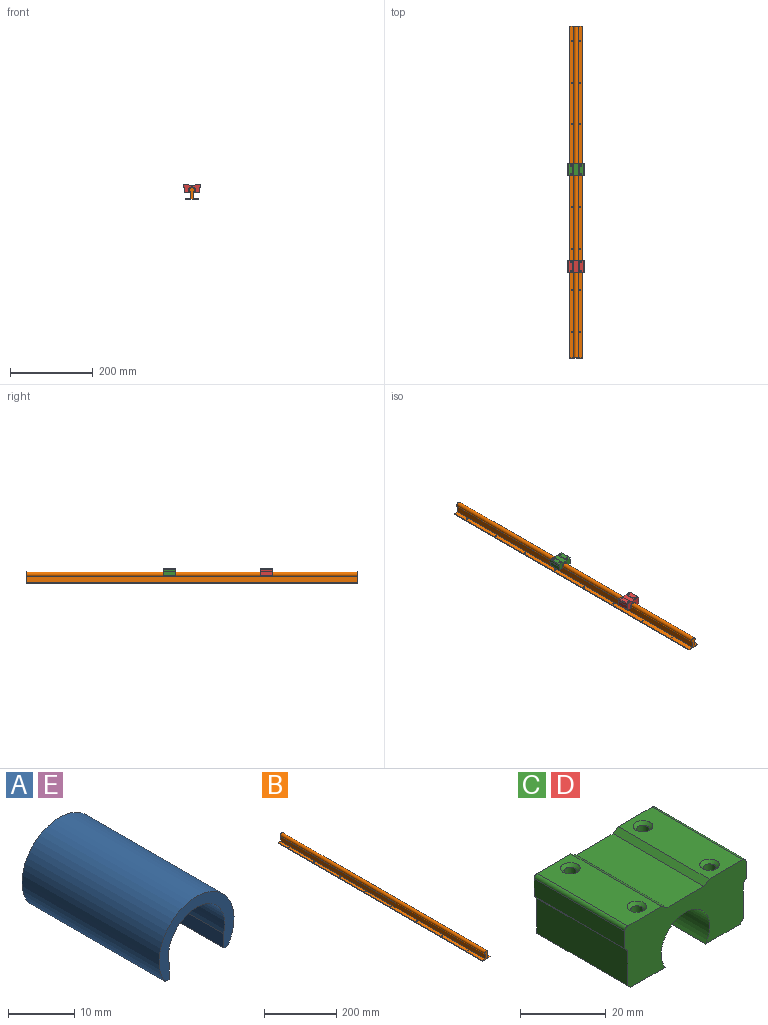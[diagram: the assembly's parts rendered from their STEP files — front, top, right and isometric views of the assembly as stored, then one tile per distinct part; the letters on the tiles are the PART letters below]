
ASSEMBLY  parts=5 mates=4
PART A: 8 faces, bbox 16x29.3x12.4 mm
  f0: cylinder r=6mm len=29.28mm, axis (0,1,0), area 655mm2, adj f2,f3,f6,f7
  f1: cylinder r=8mm len=29.28mm, axis (0,1,0), area 1009.3mm2, adj f2,f3,f4,f5
  f2: plane 16x12.41mm, normal (0,-1,0), area 59.3mm2, adj f0,f1,f4,f5,f6,f7
  f3: plane 16x12.41mm, normal (0,1,0), area 59.3mm2, adj f0,f1,f4,f5,f6,f7
  f4: plane 29.28x0.85mm, normal (0,0,-1), area 24.8mm2, adj f1,f2,f3,f6
  f5: plane 29.28x0.85mm, normal (0,0,-1), area 24.8mm2, adj f1,f2,f3,f7
  f6: plane 29.28x2.67mm, normal (-1,0,-0.03), area 78.3mm2, adj f0,f2,f3,f4
  f7: plane 29.28x2.67mm, normal (1,0,-0.03), area 78.3mm2, adj f0,f2,f3,f5
PART B: 26 faces, bbox 30x800x28 mm
  f0: cylinder r=1.5mm len=3mm, axis (0,0,1), area 18.8mm2, adj f14,f20
  f1: cylinder r=1.5mm len=3mm, axis (0,0,1), area 18.8mm2, adj f14,f20
  f2: cylinder r=1.5mm len=3mm, axis (0,0,1), area 18.8mm2, adj f14,f20
  f3: cylinder r=1.5mm len=3mm, axis (0,0,1), area 18.8mm2, adj f14,f20
  f4: cylinder r=1.5mm len=3mm, axis (0,0,1), area 18.8mm2, adj f14,f20
  f5: cylinder r=1.5mm len=3mm, axis (0,0,1), area 18.8mm2, adj f14,f20
  f6: cylinder r=1.5mm len=3mm, axis (0,0,1), area 18.8mm2, adj f14,f20
  f7: cylinder r=1.5mm len=3mm, axis (0,0,1), area 18.8mm2, adj f14,f16
  f8: cylinder r=1.5mm len=3mm, axis (0,0,1), area 18.8mm2, adj f14,f16
  f9: cylinder r=1.5mm len=3mm, axis (0,0,1), area 18.8mm2, adj f14,f16
  f10: cylinder r=1.5mm len=3mm, axis (0,0,1), area 18.8mm2, adj f14,f16
  f11: cylinder r=1.5mm len=3mm, axis (0,0,1), area 18.8mm2, adj f14,f16
  f12: cylinder r=1.5mm len=3mm, axis (0,0,1), area 18.8mm2, adj f14,f16
  f13: cylinder r=1.5mm len=3mm, axis (0,0,1), area 18.8mm2, adj f14,f16
  f14: plane 800x30mm, normal (0,0,-1), area 23886.9mm2, adj f0,f1,f2,f3,f4,f5,f6,f7
  f15: plane 800x2mm, normal (1,0,0), area 1600mm2, adj f14,f16,f22,f23
  f16: plane 800x11mm, normal (0,0,1), area 8743.5mm2, adj f7,f8,f9,f10,f11,f12,f13,f15
  f17: plane 800x15.53mm, normal (1,0,0), area 12422.3mm2, adj f16,f18,f22,f23
  f18: cylinder r=6mm len=800mm, axis (0,1,0), area 23153.9mm2, adj f17,f19,f22,f23
  f19: plane 800x15.53mm, normal (-1,0,0), area 12422.3mm2, adj f18,f20,f22,f23
  f20: plane 800x11mm, normal (0,0,1), area 8743.5mm2, adj f0,f1,f2,f3,f4,f5,f6,f19
  f21: plane 800x2mm, normal (-1,0,0), area 1600mm2, adj f14,f20,f22,f23
  f22: plane 30x28mm, normal (0,-1,0), area 288.9mm2, adj f14,f15,f16,f17,f18,f19,f20,f21
  f23: plane 30x28mm, normal (0,1,0), area 288.9mm2, adj f14,f15,f16,f17,f18,f19,f20,f21
  f24: cylinder r=1.5mm len=3mm, axis (0,0,1), area 18.8mm2, adj f14,f16
  f25: cylinder r=1.5mm len=3mm, axis (0,0,1), area 18.8mm2, adj f14,f20
PART C: 28 faces, bbox 40x30x18 mm
  f0: plane 30x11.43mm, normal (0,0,-1), area 328.9mm2, adj f1,f2,f3,f4,f23,f25
  f1: plane 40x18mm, normal (0,-1,0), area 514.1mm2, adj f0,f7,f8,f9,f10,f11,f12,f13
  f2: plane 40x18mm, normal (0,1,0), area 514.1mm2, adj f0,f7,f8,f9,f10,f11,f12,f13
  f3: cylinder r=1.5mm len=17.2mm, axis (0,0,1), area 162.1mm2, adj f0,f20
  f4: cylinder r=1.5mm len=17.2mm, axis (0,0,1), area 162.1mm2, adj f0,f19
  f5: cylinder r=1.5mm len=17.2mm, axis (0,0,1), area 162.1mm2, adj f15,f21
  f6: cylinder r=1.5mm len=17.2mm, axis (0,0,1), area 162.1mm2, adj f15,f22
  f7: plane 30x11.19mm, normal (0,0,1), area 302.3mm2, adj f1,f2,f8,f19,f20,f27
  f8: plane 30x1.71mm, normal (-0.57,0,0.82), area 62.8mm2, adj f1,f2,f7,f9
  f9: plane 30x12.2mm, normal (0,0,1), area 366mm2, adj f1,f2,f8,f10
  f10: plane 30x1.71mm, normal (0.57,0,0.82), area 62.8mm2, adj f1,f2,f9,f11
  f11: plane 30x11.19mm, normal (0,0,1), area 302.3mm2, adj f1,f2,f10,f21,f22,f26
  f12: plane 30x5mm, normal (-1,0,0), area 150mm2, adj f1,f2,f13,f26
  f13: plane 30x1mm, normal (-0.75,0,-0.66), area 40.2mm2, adj f1,f2,f12,f14
  f14: plane 30x10mm, normal (-1,0,0), area 300mm2, adj f1,f2,f13,f24
  f15: plane 30x11.43mm, normal (0,0,-1), area 328.9mm2, adj f1,f2,f5,f6,f23,f24
  f16: plane 30x10mm, normal (1,0,0), area 300mm2, adj f1,f2,f17,f25
  f17: plane 30x1mm, normal (0.75,0,-0.66), area 40.2mm2, adj f1,f2,f16,f18
  f18: plane 30x5mm, normal (1,0,0), area 150mm2, adj f1,f2,f17,f27
  f19: cone r=1.5mm half-angle=45deg, axis (0,0,1), area 13.5mm2, adj f4,f7
  f20: cone r=1.5mm half-angle=45deg, axis (0,0,1), area 13.5mm2, adj f3,f7
  f21: cone r=1.5mm half-angle=45deg, axis (0,0,1), area 13.5mm2, adj f5,f11
  f22: cone r=1.5mm half-angle=45deg, axis (0,0,1), area 13.5mm2, adj f6,f11
  f23: cylinder r=8mm len=30mm, axis (0,-1,0), area 1034.1mm2, adj f0,f1,f2,f15
  f24: plane 30x1mm, normal (-0.71,0,-0.71), area 42.4mm2, adj f1,f2,f14,f15
  f25: plane 30x1mm, normal (0.71,0,-0.71), area 42.4mm2, adj f0,f1,f2,f16
  f26: cylinder r=1mm len=30mm, axis (0,-1,0), area 47.1mm2, adj f1,f2,f11,f12
  f27: cylinder r=1mm len=30mm, axis (0,1,0), area 47.1mm2, adj f1,f2,f7,f18
PART D: same geometry as C
PART E: same geometry as A
PLACE A t=(0,53.81,0)mm
PLACE B at identity fixed
PLACE C t=(0,53.81,0)mm
PLACE D t=(0,-179.62,0)mm
PLACE E t=(0,-179.62,0)mm
MATE slider E.f0 <-> B.f18  axis (0,1,0) through (0,-179.62,-13.59)mm
MATE fastened A.f0 <-> C.f23  axis (0,1,0) through (0,53.81,-13.59)mm
MATE fastened E.f0 <-> D.f23  axis (0,1,0) through (0,-179.62,-13.59)mm
MATE slider A.f0 <-> B.f18  axis (0,1,0) through (0,53.81,-13.59)mm
